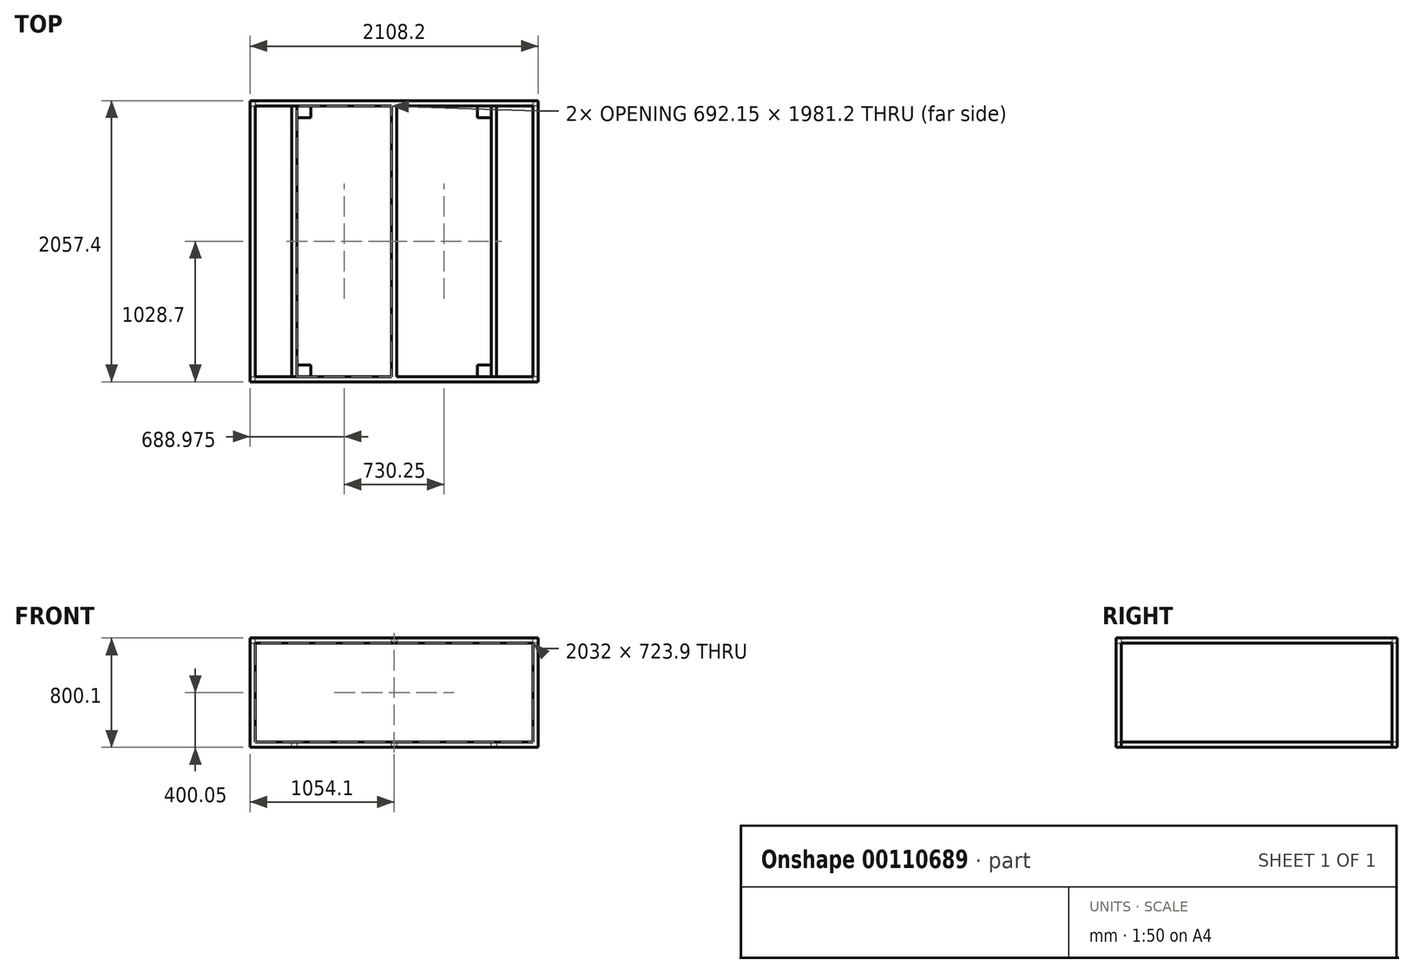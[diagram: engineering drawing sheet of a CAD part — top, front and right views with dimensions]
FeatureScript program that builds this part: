
annotation { "Feature Type Name" : "Feature", "Feature Type Description" : "" }
export const myFeature = defineFeature(function(context is Context, id is Id, definition is map)
    precondition{}
    {
        {
            var Q0;
            Q0=qCreatedBy(makeId("Right.planeOp"),FACE);
            var sketch = newSketch(context, id + "F0", { "sketchPlane" : qUnion([Q0])});
            skLineSegment(sketch, "E0", {"start": v(990.6, 0) * mm, "end": v(1028.7, 0) * mm});
            skLineSegment(sketch, "E1", {"start": v(1028.7, 0) * mm, "end": v(1028.7, 800.1) * mm});
            skLineSegment(sketch, "E2", {"start": v(1028.7, 800.1) * mm, "end": v(0, 800.1) * mm});
            skLineSegment(sketch, "E3.0", {"start": v(990.6, 762) * mm, "end": v(0, 762) * mm});
            skLineSegment(sketch, "E3.1", {"start": v(990.6, 0) * mm, "end": v(990.6, 762) * mm});
            skLineSegment(sketch, "E4.MirrorCS", {"start": v(-990.6, 0) * mm, "end": v(-1028.7, 0) * mm});
            skLineSegment(sketch, "E5.MirrorCS", {"start": v(-1028.7, 0) * mm, "end": v(-1028.7, 800.1) * mm});
            skLineSegment(sketch, "E6.MirrorCS", {"start": v(-1028.7, 800.1) * mm, "end": v(0, 800.1) * mm});
            skLineSegment(sketch, "E7.MirrorCS", {"start": v(-990.6, 762) * mm, "end": v(0, 762) * mm});
            skLineSegment(sketch, "E8.MirrorCS", {"start": v(-990.6, 0) * mm, "end": v(-990.6, 762) * mm});
            skPoint(sketch, "E9.orphan", {"position": v(0, 0) * mm});
            skPoint(sketch, "E3.2.start.orphan", {"position": v(0, 38.1) * mm});
            skSolve(sketch);
        }
        {
            var Q0;
            Q0 = qSketchRegion(id + "F0", true);
            extrude(context, id + "F1", {"entities" : qUnion([Q0]), "depth" : 38.1 * mm});
        }
        {
            var Q0;
            Q0=qCreatedBy(makeId("Right.planeOp"),FACE);
            cPlane(context, id + "F2", {"entities" : qUnion([Q0]), "cplaneType" : CPlaneType.OFFSET, "offset" : 1016 * mm, "oppositeDirection" : true, "width" : 152.4 * mm, "height" : 152.4 * mm});
        }
        {
            var Q0;
            Q0=makeQuery(id+"F1.opExtrude","SWEPT_BODY",BODY,{"disambiguationData":[OSD([sQuery(id+"F0.wireOp",EDGE,"E0"),sQuery(id+"F0.wireOp",EDGE,"E1"),sQuery(id+"F0.wireOp",EDGE,"E2"),sQuery(id+"F0.wireOp",EDGE,"E3.0"),sQuery(id+"F0.wireOp",EDGE,"E3.1"),sQuery(id+"F0.wireOp",EDGE,"E4.MirrorCS"),sQuery(id+"F0.wireOp",EDGE,"E5.MirrorCS"),sQuery(id+"F0.wireOp",EDGE,"E6.MirrorCS"),sQuery(id+"F0.wireOp",EDGE,"E7.MirrorCS"),sQuery(id+"F0.wireOp",EDGE,"E8.MirrorCS")])]});
            var Q1;
            Q1=qCreatedBy(id+"F2.planeOp",FACE);
            mirror(context, id + "F3", {"entities" : qUnion([Q0]), "mirrorPlane" : qUnion([Q1])});
        }
        {
            var Q0;
            Q0=qCreatedBy(makeId("Right.planeOp"),FACE);
            var sketch = newSketch(context, id + "F4", { "sketchPlane" : qUnion([Q0])});
            skLineSegment(sketch, "E10.0", {"start": v(1028.7, 800.1) * mm, "end": v(990.6, 800.1) * mm});
            skLineSegment(sketch, "E11", {"start": v(-1028.7, 800.1) * mm, "end": v(-1028.7, 762) * mm});
            skLineSegment(sketch, "E12", {"start": v(-1028.7, 762) * mm, "end": v(-990.6, 762) * mm});
            skLineSegment(sketch, "E13", {"start": v(-990.6, 762) * mm, "end": v(-990.6, 800.1) * mm});
            skLineSegment(sketch, "E14", {"start": v(1028.7, 800.1) * mm, "end": v(1028.7, 762) * mm});
            skLineSegment(sketch, "E15", {"start": v(1028.7, 762) * mm, "end": v(990.6, 762) * mm});
            skLineSegment(sketch, "E16", {"start": v(990.6, 762) * mm, "end": v(990.6, 800.1) * mm});
            skLineSegment(sketch, "E17.trimOffspring", {"start": v(-990.6, 800.1) * mm, "end": v(-1028.7, 800.1) * mm});
            skLineSegment(sketch, "E18.0", {"start": v(-990.6, 0) * mm, "end": v(-1028.7, 0) * mm});
            skLineSegment(sketch, "E19", {"start": v(-1028.7, 0) * mm, "end": v(-1028.7, 38.1) * mm});
            skLineSegment(sketch, "E20", {"start": v(-1028.7, 38.1) * mm, "end": v(-990.6, 38.1) * mm});
            skLineSegment(sketch, "E21", {"start": v(-990.6, 0) * mm, "end": v(-990.6, 38.1) * mm});
            skLineSegment(sketch, "E22.MirrorCS", {"start": v(1028.7, 0) * mm, "end": v(1028.7, 38.1) * mm});
            skLineSegment(sketch, "E23.MirrorCS", {"start": v(1028.7, 38.1) * mm, "end": v(990.6, 38.1) * mm});
            skLineSegment(sketch, "E24.MirrorCS", {"start": v(990.6, 0) * mm, "end": v(990.6, 38.1) * mm});
            skLineSegment(sketch, "E25.MirrorCS", {"start": v(990.6, 0) * mm, "end": v(1028.7, 0) * mm});
            skSolve(sketch);
        }
        {
            var Q0;
            Q0 = qSketchRegion(id + "F4", true);
            var Q1;
            Q1=makeQuery(id+"F3.opPattern","COPY",FACE,{"derivedFrom":makeQuery(id+"F1.opExtrude","CAP_FACE",FACE,{"disambiguationData":[OSD([sQuery(id+"F0.wireOp",EDGE,"E0"),sQuery(id+"F0.wireOp",EDGE,"E1"),sQuery(id+"F0.wireOp",EDGE,"E2"),sQuery(id+"F0.wireOp",EDGE,"E3.0"),sQuery(id+"F0.wireOp",EDGE,"E3.1"),sQuery(id+"F0.wireOp",EDGE,"E4.MirrorCS"),sQuery(id+"F0.wireOp",EDGE,"E5.MirrorCS"),sQuery(id+"F0.wireOp",EDGE,"E6.MirrorCS"),sQuery(id+"F0.wireOp",EDGE,"E7.MirrorCS"),sQuery(id+"F0.wireOp",EDGE,"E8.MirrorCS")])],"isStart":true}),"instanceName":"1"});
            extrude(context, id + "F5", {"entities" : qUnion([Q0]), "operationType" : NewBodyOperationType.ADD, "endBound" : BoundingType.UP_TO_SURFACE, "oppositeDirection" : true, "endBoundEntityFace" : qUnion([Q1]), "depth" : 25.4 * mm});
        }
        {
            var Q0;
            {var subQ0=makeQuery(id+"F1.opExtrude","SWEPT_FACE",FACE,{"disambiguationData":[OSD([sQuery(id+"F0.wireOp",EDGE,"E5.MirrorCS")])]});Q0=makeQuery(id+"F5.boolean.opBoolean","MERGE",FACE,{"derivedFrom":[subQ0,makeQuery(id+"F3.opPattern","COPY",FACE,{"derivedFrom":subQ0,"instanceName":"1"}),makeQuery(id+"F5.opExtrude","SWEPT_FACE",FACE,{"disambiguationData":[OSD([sQuery(id+"F4.wireOp",EDGE,"OlDpZHyJ-owGB-hcmZ-Z4MX-y5TkGbtLBd3H")])]}),makeQuery(id+"F5.opExtrude","SWEPT_FACE",FACE,{"disambiguationData":[OSD([sQuery(id+"F4.wireOp",EDGE,"E11")])]})]});}
            cPlane(context, id + "F6", {"entities" : qUnion([Q0]), "cplaneType" : CPlaneType.OFFSET, "offset" : 0 * mm, "width" : 152.4 * mm, "height" : 152.4 * mm});
        }
        {
            var Q0;
            Q0=qCreatedBy(id+"F6.planeOp",FACE);
            var sketch = newSketch(context, id + "F7", { "sketchPlane" : qUnion([Q0])});
            skLineSegment(sketch, "E26.0", {"start": v(38.1, 0) * mm, "end": v(38.1, 800.1) * mm, "construction": true});
            skLineSegment(sketch, "E27.0", {"start": v(-266.7, 0) * mm, "end": v(-266.7, 38.1) * mm});
            skLineSegment(sketch, "E28", {"start": v(-266.7, 0) * mm, "end": v(-304.8, 0) * mm});
            skLineSegment(sketch, "E29", {"start": v(-304.8, 0) * mm, "end": v(-304.8, 38.1) * mm});
            skLineSegment(sketch, "E30", {"start": v(-304.8, 38.1) * mm, "end": v(-266.7, 38.1) * mm});
            skLineSegment(sketch, "E31.0", {"start": v(-996.95, 762) * mm, "end": v(-996.95, 800.1) * mm});
            skLineSegment(sketch, "E32.0", {"start": v(-1035.05, 762) * mm, "end": v(-996.95, 762) * mm});
            skLineSegment(sketch, "E33.MirrorCS", {"start": v(-1765.3, 0) * mm, "end": v(-1765.3, 38.1) * mm});
            skLineSegment(sketch, "E34.MirrorCS", {"start": v(-1765.3, 0) * mm, "end": v(-1727.2, 0) * mm});
            skLineSegment(sketch, "E35.MirrorCS", {"start": v(-1727.2, 0) * mm, "end": v(-1727.2, 38.1) * mm});
            skLineSegment(sketch, "E36.MirrorCS", {"start": v(-1727.2, 38.1) * mm, "end": v(-1765.3, 38.1) * mm});
            skLineSegment(sketch, "E37", {"start": v(-1035.05, 38.1) * mm, "end": v(-1035.05, 0) * mm});
            skLineSegment(sketch, "E38", {"start": v(-1035.05, 0) * mm, "end": v(-996.95, 0) * mm});
            skLineSegment(sketch, "E39", {"start": v(-996.95, 0) * mm, "end": v(-996.95, 38.1) * mm});
            skLineSegment(sketch, "E40", {"start": v(-996.95, 38.1) * mm, "end": v(-1035.05, 38.1) * mm});
            skLineSegment(sketch, "E41", {"start": v(-1035.05, 762) * mm, "end": v(-1035.05, 800.1) * mm});
            skLineSegment(sketch, "E42", {"start": v(-1035.05, 800.1) * mm, "end": v(-996.95, 800.1) * mm});
            skSolve(sketch);
        }
        {
            var Q0;
            Q0 = qSketchRegion(id + "F7", true);
            var Q1;
            {var subQ0=makeQuery(id+"F1.opExtrude","SWEPT_FACE",FACE,{"disambiguationData":[OSD([sQuery(id+"F0.wireOp",EDGE,"E3.1")])]});Q1=makeQuery(id+"F5.boolean.opBoolean","MERGE",FACE,{"derivedFrom":[subQ0,makeQuery(id+"F3.opPattern","COPY",FACE,{"derivedFrom":subQ0,"instanceName":"1"}),makeQuery(id+"F5.opExtrude","SWEPT_FACE",FACE,{"disambiguationData":[OSD([sQuery(id+"F4.wireOp",EDGE,"fnpsByQn-PNxE-PRlT-7g02-5BAe7V87WMuu")])]})]});}
            extrude(context, id + "F8", {"entities" : qUnion([Q0]), "operationType" : NewBodyOperationType.ADD, "endBound" : BoundingType.UP_TO_SURFACE, "oppositeDirection" : true, "endBoundEntityFace" : qUnion([Q1]), "depth" : 25.4 * mm});
        }
        {
            var Q0;
            Q0=qCreatedBy(makeId("Top.planeOp"),FACE);
            var sketch = newSketch(context, id + "F9", { "sketchPlane" : qUnion([Q0])});
            skLineSegment(sketch, "E43.0", {"start": v(-1727.2, -904.87) * mm, "end": v(-1727.2, -990.6) * mm});
            skLineSegment(sketch, "E44", {"start": v(-1727.2, -990.6) * mm, "end": v(-1627.19, -990.6) * mm});
            skLineSegment(sketch, "E45", {"start": v(-1627.19, -990.6) * mm, "end": v(-1627.19, -904.87) * mm});
            skLineSegment(sketch, "E46", {"start": v(-1627.19, -904.87) * mm, "end": v(-1727.2, -904.87) * mm});
            skLineSegment(sketch, "E47.0", {"start": v(-1727.2, 990.6) * mm, "end": v(-1727.2, 904.87) * mm});
            skLineSegment(sketch, "E48", {"start": v(-1727.2, 990.6) * mm, "end": v(-1627.19, 990.6) * mm});
            skLineSegment(sketch, "E49", {"start": v(-1627.19, 990.6) * mm, "end": v(-1627.19, 904.87) * mm});
            skLineSegment(sketch, "E50", {"start": v(-1627.19, 904.87) * mm, "end": v(-1727.2, 904.87) * mm});
            skLineSegment(sketch, "E51.MirrorCS", {"start": v(-304.8, -904.87) * mm, "end": v(-304.8, -990.6) * mm});
            skLineSegment(sketch, "E52.MirrorCS", {"start": v(-404.81, -990.6) * mm, "end": v(-404.81, -904.87) * mm});
            skLineSegment(sketch, "E53.MirrorCS", {"start": v(-304.8, -990.6) * mm, "end": v(-404.81, -990.6) * mm});
            skLineSegment(sketch, "E54.MirrorCS", {"start": v(-404.81, -904.87) * mm, "end": v(-304.8, -904.87) * mm});
            skLineSegment(sketch, "E55.MirrorCS", {"start": v(-304.8, 990.6) * mm, "end": v(-404.81, 990.6) * mm});
            skLineSegment(sketch, "E56.MirrorCS", {"start": v(-304.8, 990.6) * mm, "end": v(-304.8, 904.87) * mm});
            skLineSegment(sketch, "E57.MirrorCS", {"start": v(-404.81, 990.6) * mm, "end": v(-404.81, 904.87) * mm});
            skLineSegment(sketch, "E58.MirrorCS", {"start": v(-404.81, 904.87) * mm, "end": v(-304.8, 904.87) * mm});
            skSolve(sketch);
        }
        {
            var Q0;
            Q0 = qSketchRegion(id + "F9", true);
            extrude(context, id + "F10", {"entities" : qUnion([Q0]), "operationType" : NewBodyOperationType.ADD, "depth" : 1.52 * mm});
        }
    });
